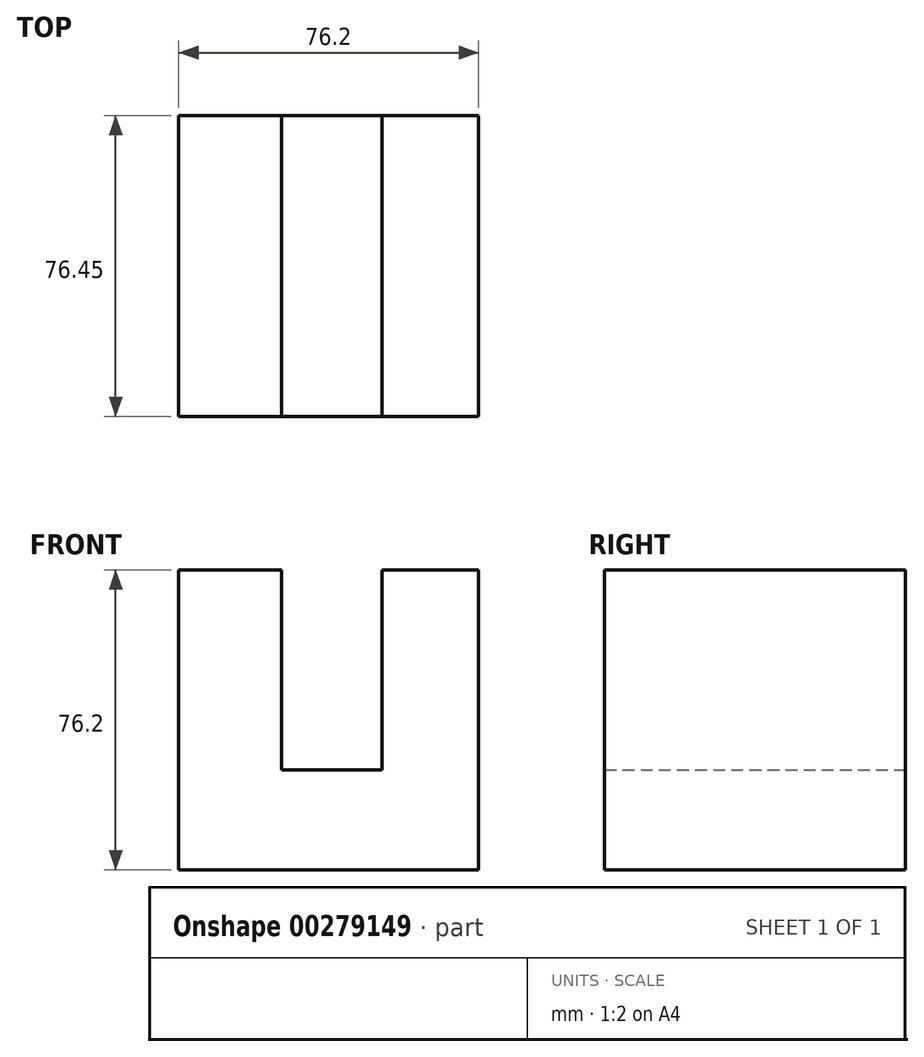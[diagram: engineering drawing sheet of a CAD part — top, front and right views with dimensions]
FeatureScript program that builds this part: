
annotation { "Feature Type Name" : "Feature", "Feature Type Description" : "" }
export const myFeature = defineFeature(function(context is Context, id is Id, definition is map)
    precondition{}
    {
        {
            var Q0;
            Q0=qCreatedBy(makeId("Front.planeOp"),FACE);
            var sketch = newSketch(context, id + "F0", { "sketchPlane" : qUnion([Q0])});
            skLineSegment(sketch, "E0", {"start": v(-51.6, 73.43) * mm, "end": v(-51.6, -2.77) * mm});
            skLineSegment(sketch, "E1", {"start": v(-51.6, -2.77) * mm, "end": v(24.6, -2.77) * mm});
            skLineSegment(sketch, "E2", {"start": v(24.6, -2.77) * mm, "end": v(24.6, 73.43) * mm});
            skLineSegment(sketch, "E3", {"start": v(24.6, 73.43) * mm, "end": v(0, 73.43) * mm});
            skLineSegment(sketch, "E4", {"start": v(-51.6, 73.43) * mm, "end": v(-25.4, 73.43) * mm});
            skLineSegment(sketch, "E5", {"start": v(-25.4, 73.43) * mm, "end": v(-25.4, 22.63) * mm});
            skLineSegment(sketch, "E6", {"start": v(0, 22.63) * mm, "end": v(-25.4, 22.63) * mm});
            skLineSegment(sketch, "E7", {"start": v(0, 22.63) * mm, "end": v(0, 73.43) * mm});
            skSolve(sketch);
        }
        {
            var Q0;
            Q0 = qSketchRegion(id + "F0", true);
            extrude(context, id + "F1", {"entities" : qUnion([Q0]), "depth" : 76.45 * mm});
        }
    });
